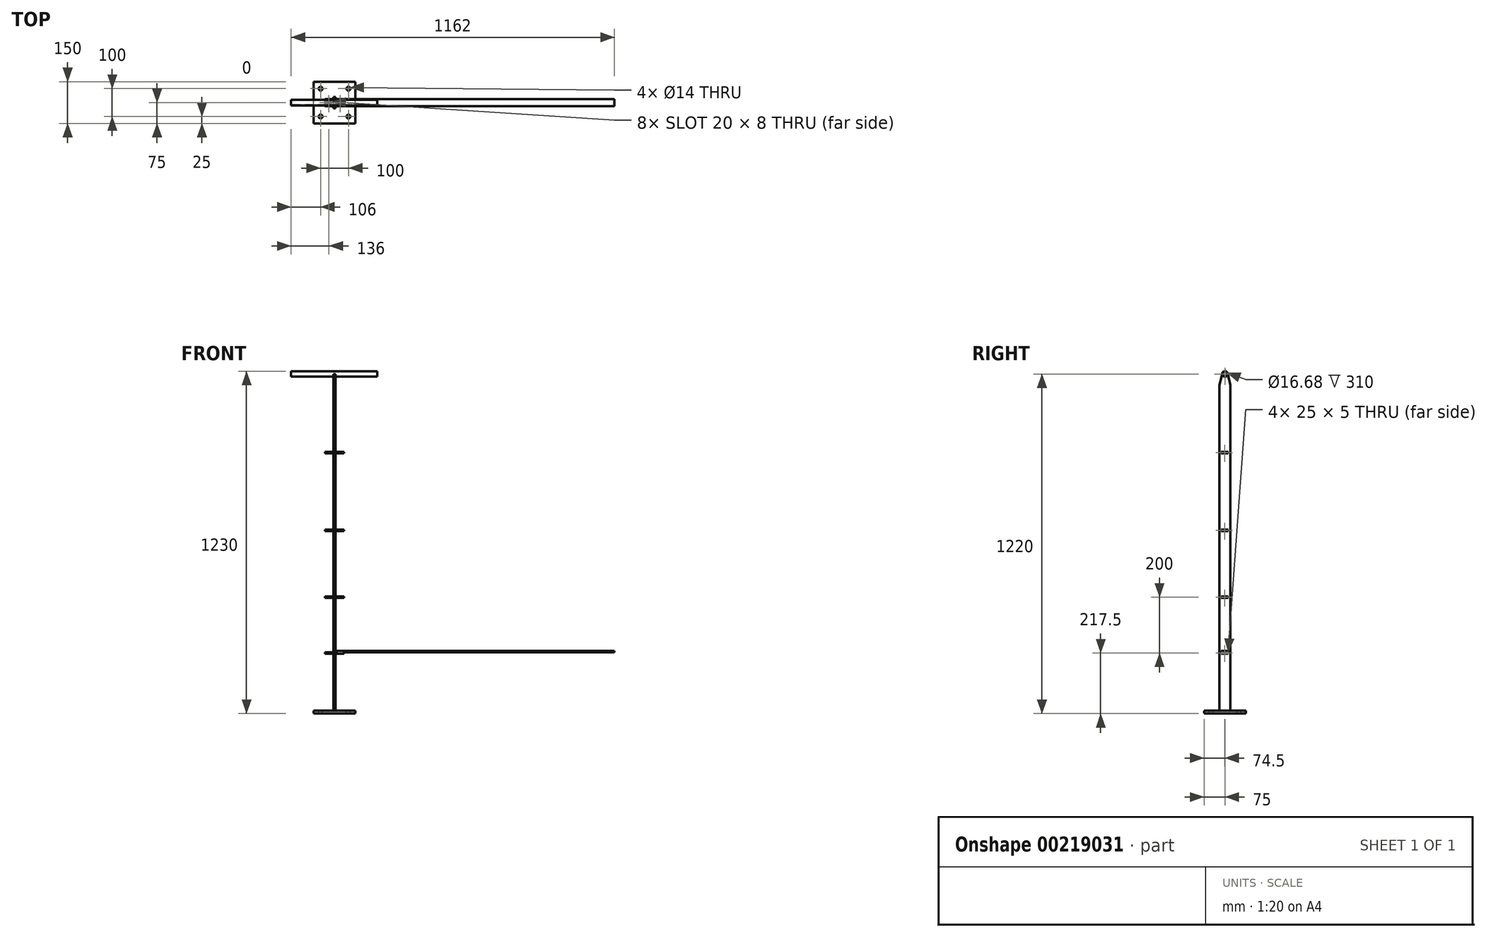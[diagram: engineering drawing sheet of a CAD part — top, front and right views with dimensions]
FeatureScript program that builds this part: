
annotation { "Feature Type Name" : "Feature", "Feature Type Description" : "" }
export const myFeature = defineFeature(function(context is Context, id is Id, definition is map)
    precondition{}
    {
        {
            var Q0;
            Q0=qCreatedBy(makeId("Top.planeOp"),FACE);
            var sketch = newSketch(context, id + "F0", { "sketchPlane" : qUnion([Q0])});
            skLineSegment(sketch, "E0.bottom", {"start": v(75, -75) * mm, "end": v(-75, -75) * mm});
            skLineSegment(sketch, "E0.top", {"start": v(75, 75) * mm, "end": v(-75, 75) * mm});
            skLineSegment(sketch, "E0.left", {"start": v(75, -75) * mm, "end": v(75, 75) * mm});
            skLineSegment(sketch, "E0.right", {"start": v(-75, -75) * mm, "end": v(-75, 75) * mm});
            skPoint(sketch, "E0.middle", {"position": v(0, 0) * mm});
            skSolve(sketch);
        }
        {
            var Q0;
            Q0 = qSketchRegion(id + "F0", true);
            extrude(context, id + "F1", {"entities" : qUnion([Q0]), "depth" : 10 * mm});
        }
        {
            var Q0;
            Q0=makeQuery(id+"F1.opExtrude","CAP_FACE",FACE,{"disambiguationData":[OSD([sQuery(id+"F0.wireOp",EDGE,"E0.bottom"),sQuery(id+"F0.wireOp",EDGE,"E0.top"),sQuery(id+"F0.wireOp",EDGE,"E0.left"),sQuery(id+"F0.wireOp",EDGE,"E0.right")])],"isStart":false});
            var sketch = newSketch(context, id + "F2", { "sketchPlane" : qUnion([Q0])});
            skLineSegment(sketch, "E1.bottom", {"start": v(4, -20) * mm, "end": v(-4, -20) * mm});
            skLineSegment(sketch, "E1.top", {"start": v(4, 20) * mm, "end": v(-4, 20) * mm});
            skLineSegment(sketch, "E1.left", {"start": v(4, -20) * mm, "end": v(4, 20) * mm});
            skLineSegment(sketch, "E1.right", {"start": v(-4, -20) * mm, "end": v(-4, 20) * mm});
            skPoint(sketch, "E1.middle", {"position": v(0, 0) * mm});
            skSolve(sketch);
        }
        {
            var Q0;
            Q0 = qSketchRegion(id + "F2", true);
            extrude(context, id + "F3", {"entities" : qUnion([Q0]), "operationType" : NewBodyOperationType.ADD, "depth" : 1210 * mm});
        }
        {
            var Q0;
            Q0=makeQuery(id+"F3.opExtrude","SWEPT_FACE",FACE,{"disambiguationData":[OSD([sQuery(id+"F2.wireOp",EDGE,"E1.left")])]});
            var sketch = newSketch(context, id + "F4", { "sketchPlane" : qUnion([Q0])});
            skLineSegment(sketch, "E2.bottom", {"start": v(-13, 215) * mm, "end": v(12, 215) * mm});
            skLineSegment(sketch, "E2.top", {"start": v(-13, 220) * mm, "end": v(12, 220) * mm});
            skLineSegment(sketch, "E2.left", {"start": v(-13, 215) * mm, "end": v(-13, 220) * mm});
            skLineSegment(sketch, "E2.right", {"start": v(12, 215) * mm, "end": v(12, 220) * mm});
            skSolve(sketch);
        }
        {
            var Q0;
            Q0 = qSketchRegion(id + "F4", true);
            extrude(context, id + "F5", {"entities" : qUnion([Q0]), "depth" : 30 * mm});
        }
        {
            var Q0;
            Q0=makeQuery(id+"F5.opExtrude","SWEPT_FACE",FACE,{"disambiguationData":[OSD([sQuery(id+"F4.wireOp",EDGE,"E2.top")])]});
            var sketch = newSketch(context, id + "F6", { "sketchPlane" : qUnion([Q0])});
            skArc(sketch, "E3", {"start": v(26, -4) * mm, "mid": v(30, 0) * mm, "end": v(26, 4) * mm});
            skArc(sketch, "E4", {"start": v(14, 4) * mm, "mid": v(10, 0) * mm, "end": v(14, -4) * mm});
            skLineSegment(sketch, "E5", {"start": v(14, 4) * mm, "end": v(26, 4) * mm});
            skLineSegment(sketch, "E6", {"start": v(26, -4) * mm, "end": v(14, -4) * mm});
            skSolve(sketch);
        }
        {
            var Q0;
            Q0 = qSketchRegion(id + "F6", true);
            extrude(context, id + "F7", {"entities" : qUnion([Q0]), "operationType" : NewBodyOperationType.REMOVE, "oppositeDirection" : true, "depth" : 25 * mm});
        }
        {
            var Q0;
            Q0=makeQuery(id+"F5.opExtrude","SWEPT_FACE",FACE,{"disambiguationData":[OSD([sQuery(id+"F4.wireOp",EDGE,"E2.top")])]});
            var sketch = newSketch(context, id + "F8", { "sketchPlane" : qUnion([Q0])});
            skLineSegment(sketch, "E7.bottom", {"start": v(6, 12) * mm, "end": v(1006, 12) * mm});
            skLineSegment(sketch, "E7.top", {"start": v(6, -13) * mm, "end": v(1006, -13) * mm});
            skLineSegment(sketch, "E7.left", {"start": v(6, 12) * mm, "end": v(6, -13) * mm});
            skLineSegment(sketch, "E7.right", {"start": v(1006, 12) * mm, "end": v(1006, -13) * mm});
            skArc(sketch, "E8", {"start": v(14, 4) * mm, "mid": v(10, 0) * mm, "end": v(14, -4) * mm});
            skArc(sketch, "E9", {"start": v(26, -4) * mm, "mid": v(30, 0) * mm, "end": v(26, 4) * mm});
            skLineSegment(sketch, "E10", {"start": v(14, 4) * mm, "end": v(26, 4) * mm});
            skLineSegment(sketch, "E11", {"start": v(14, -4) * mm, "end": v(26, -4) * mm});
            skSolve(sketch);
        }
        {
            var Q0;
            Q0 = qSketchRegion(id + "F8", true);
            extrude(context, id + "F9", {"entities" : qUnion([Q0]), "depth" : 5 * mm});
        }
        {
            var Q0;
            Q0=makeQuery(id+"F5.opExtrude","SWEPT_FACE",FACE,{"disambiguationData":[OSD([sQuery(id+"F4.wireOp",EDGE,"E2.top")])]});
            var sketch = newSketch(context, id + "F10", { "sketchPlane" : qUnion([Q0])});
            skArc(sketch, "E12", {"start": v(14, 4) * mm, "mid": v(10, 0) * mm, "end": v(14, -4) * mm});
            skArc(sketch, "E13", {"start": v(26, -4) * mm, "mid": v(30, 0) * mm, "end": v(26, 4) * mm});
            skLineSegment(sketch, "E14", {"start": v(14, 4) * mm, "end": v(26, 4) * mm});
            skLineSegment(sketch, "E15", {"start": v(14, -4) * mm, "end": v(26, -4) * mm});
            skSolve(sketch);
        }
        {
            var Q0;
            Q0 = qSketchRegion(id + "F10", true);
            extrude(context, id + "F11", {"entities" : qUnion([Q0]), "operationType" : NewBodyOperationType.REMOVE, "oppositeDirection" : true, "depth" : 25 * mm});
        }
        {
            var Q0;
            Q0=makeQuery(id+"F1.opExtrude","CAP_FACE",FACE,{"disambiguationData":[OSD([sQuery(id+"F0.wireOp",EDGE,"E0.bottom"),sQuery(id+"F0.wireOp",EDGE,"E0.top"),sQuery(id+"F0.wireOp",EDGE,"E0.left"),sQuery(id+"F0.wireOp",EDGE,"E0.right")])],"isStart":false});
            var sketch = newSketch(context, id + "F12", { "sketchPlane" : qUnion([Q0])});
            skCircle(sketch, "E16", {"center": v(-50, 50) * mm, "radius": 7 * mm});
            skCircle(sketch, "E17.MirrorC", {"center": v(50, 50) * mm, "radius": 7 * mm});
            skCircle(sketch, "E18.MirrorC", {"center": v(-50, -50) * mm, "radius": 7 * mm});
            skCircle(sketch, "E19.MirrorC", {"center": v(50, -50) * mm, "radius": 7 * mm});
            skSolve(sketch);
        }
        {
            var Q0;
            Q0=makeQuery(id+"F5.opExtrude","SWEPT_BODY",BODY,{"disambiguationData":[OSD([sQuery(id+"F4.wireOp",EDGE,"E2.bottom"),sQuery(id+"F4.wireOp",EDGE,"E2.top"),sQuery(id+"F4.wireOp",EDGE,"E2.left"),sQuery(id+"F4.wireOp",EDGE,"E2.right")])]});
            transform(context, id + "F13", {"entities" : qUnion([Q0]), "transformType" : TransformType.TRANSLATION_3D, "dx" : 0 * mm, "dy" : 0 * mm, "dz" : 200 * mm, "makeCopy" : true});
        }
        {
            var Q0;
            Q0=makeQuery(id+"F5.opExtrude","SWEPT_BODY",BODY,{"disambiguationData":[OSD([sQuery(id+"F4.wireOp",EDGE,"E2.bottom"),sQuery(id+"F4.wireOp",EDGE,"E2.top"),sQuery(id+"F4.wireOp",EDGE,"E2.left"),sQuery(id+"F4.wireOp",EDGE,"E2.right")])]});
            transform(context, id + "F14", {"entities" : qUnion([Q0]), "transformType" : TransformType.TRANSLATION_3D, "dx" : 0 * mm, "dy" : 0 * mm, "dz" : 440 * mm, "makeCopy" : true});
        }
        {
            var Q0;
            Q0=makeQuery(id+"F5.opExtrude","SWEPT_BODY",BODY,{"disambiguationData":[OSD([sQuery(id+"F4.wireOp",EDGE,"E2.bottom"),sQuery(id+"F4.wireOp",EDGE,"E2.top"),sQuery(id+"F4.wireOp",EDGE,"E2.left"),sQuery(id+"F4.wireOp",EDGE,"E2.right")])]});
            transform(context, id + "F15", {"entities" : qUnion([Q0]), "transformType" : TransformType.TRANSLATION_3D, "dx" : 0 * mm, "dy" : 0 * mm, "dz" : 720 * mm, "makeCopy" : true});
        }
        {
            var Q0;
            Q0=makeQuery(id+"F5.opExtrude","SWEPT_BODY",BODY,{"disambiguationData":[OSD([sQuery(id+"F4.wireOp",EDGE,"E2.bottom"),sQuery(id+"F4.wireOp",EDGE,"E2.top"),sQuery(id+"F4.wireOp",EDGE,"E2.left"),sQuery(id+"F4.wireOp",EDGE,"E2.right")])]});
            var Q1;
            Q1=makeQuery(id+"F15.opPattern","COPY",BODY,{"derivedFrom":makeQuery(id+"F5.opExtrude","SWEPT_BODY",BODY,{"disambiguationData":[OSD([sQuery(id+"F4.wireOp",EDGE,"E2.bottom"),sQuery(id+"F4.wireOp",EDGE,"E2.top"),sQuery(id+"F4.wireOp",EDGE,"E2.left"),sQuery(id+"F4.wireOp",EDGE,"E2.right")])]}),"instanceName":"1"});
            var Q2;
            Q2=makeQuery(id+"F14.opPattern","COPY",BODY,{"derivedFrom":makeQuery(id+"F5.opExtrude","SWEPT_BODY",BODY,{"disambiguationData":[OSD([sQuery(id+"F4.wireOp",EDGE,"E2.bottom"),sQuery(id+"F4.wireOp",EDGE,"E2.top"),sQuery(id+"F4.wireOp",EDGE,"E2.left"),sQuery(id+"F4.wireOp",EDGE,"E2.right")])]}),"instanceName":"1"});
            var Q3;
            Q3=makeQuery(id+"F13.opPattern","COPY",BODY,{"derivedFrom":makeQuery(id+"F5.opExtrude","SWEPT_BODY",BODY,{"disambiguationData":[OSD([sQuery(id+"F4.wireOp",EDGE,"E2.bottom"),sQuery(id+"F4.wireOp",EDGE,"E2.top"),sQuery(id+"F4.wireOp",EDGE,"E2.left"),sQuery(id+"F4.wireOp",EDGE,"E2.right")])]}),"instanceName":"1"});
            var Q4;
            Q4=qCreatedBy(makeId("Right.planeOp"),FACE);
            mirror(context, id + "F16", {"operationType" : NewBodyOperationType.ADD, "entities" : qUnion([Q0, Q1, Q2, Q3]), "mirrorPlane" : qUnion([Q4])});
        }
        {
            var Q0;
            Q0=makeQuery(id+"F4.imprint","IMPRINT",FACE,{"disambiguationData":[TD([[makeQuery(id+"F4.imprint","IMPRINT",EDGE,{"derivedFrom":sQuery(id+"F4.wireOp",EDGE,"E2.bottom")}),-1.0]])]});
            var sketch = newSketch(context, id + "F17", { "sketchPlane" : qUnion([Q0])});
            skCircle(sketch, "E20", {"center": v(0, 1220) * mm, "radius": 10 * mm});
            skLineSegment(sketch, "E21", {"start": v(-10, 1220.11) * mm, "end": v(-20, 1180) * mm});
            skLineSegment(sketch, "E22", {"start": v(0, 1220) * mm, "end": v(0, 1236.62) * mm, "construction": true});
            skLineSegment(sketch, "E23.MirrorCS", {"start": v(10, 1220.11) * mm, "end": v(20, 1180) * mm});
            skLineSegment(sketch, "E24", {"start": v(20, 1180) * mm, "end": v(26.73, 1180) * mm});
            skLineSegment(sketch, "E25", {"start": v(26.73, 1180) * mm, "end": v(26.73, 1235.38) * mm});
            skLineSegment(sketch, "E26", {"start": v(26.73, 1235.38) * mm, "end": v(-23.26, 1235.38) * mm});
            skLineSegment(sketch, "E27", {"start": v(-23.26, 1235.38) * mm, "end": v(-23.26, 1180) * mm});
            skLineSegment(sketch, "E28", {"start": v(-23.26, 1180) * mm, "end": v(-20, 1180) * mm});
            skSolve(sketch);
        }
        {
            var Q0;
            Q0 = qSketchRegion(id + "F17", true);
            extrude(context, id + "F18", {"entities" : qUnion([Q0]), "operationType" : NewBodyOperationType.REMOVE, "oppositeDirection" : true, "depth" : 25 * mm});
        }
        {
            var Q0;
            Q0=makeQuery(id+"F4.imprint","IMPRINT",FACE,{"disambiguationData":[TD([[makeQuery(id+"F4.imprint","IMPRINT",EDGE,{"derivedFrom":sQuery(id+"F4.wireOp",EDGE,"E2.bottom")}),-1.0]])]});
            var sketch = newSketch(context, id + "F19", { "sketchPlane" : qUnion([Q0])});
            skCircle(sketch, "E29", {"center": v(0, 1220) * mm, "radius": 10 * mm});
            skCircle(sketch, "E30", {"center": v(0, 1220) * mm, "radius": 8.34 * mm});
            skSolve(sketch);
        }
        {
            var Q0;
            Q0 = qSketchRegion(id + "F19", true);
            extrude(context, id + "F20", {"entities" : qUnion([Q0]), "operationType" : NewBodyOperationType.ADD, "depth" : 150 * mm, "hasSecondDirection" : true, "secondDirectionOppositeDirection" : true, "secondDirectionDepth" : 160 * mm});
        }
        {
            var Q0;
            Q0 = qSketchRegion(id + "F12", true);
            extrude(context, id + "F21", {"entities" : qUnion([Q0]), "operationType" : NewBodyOperationType.REMOVE, "oppositeDirection" : true, "depth" : 25 * mm});
        }
    });
